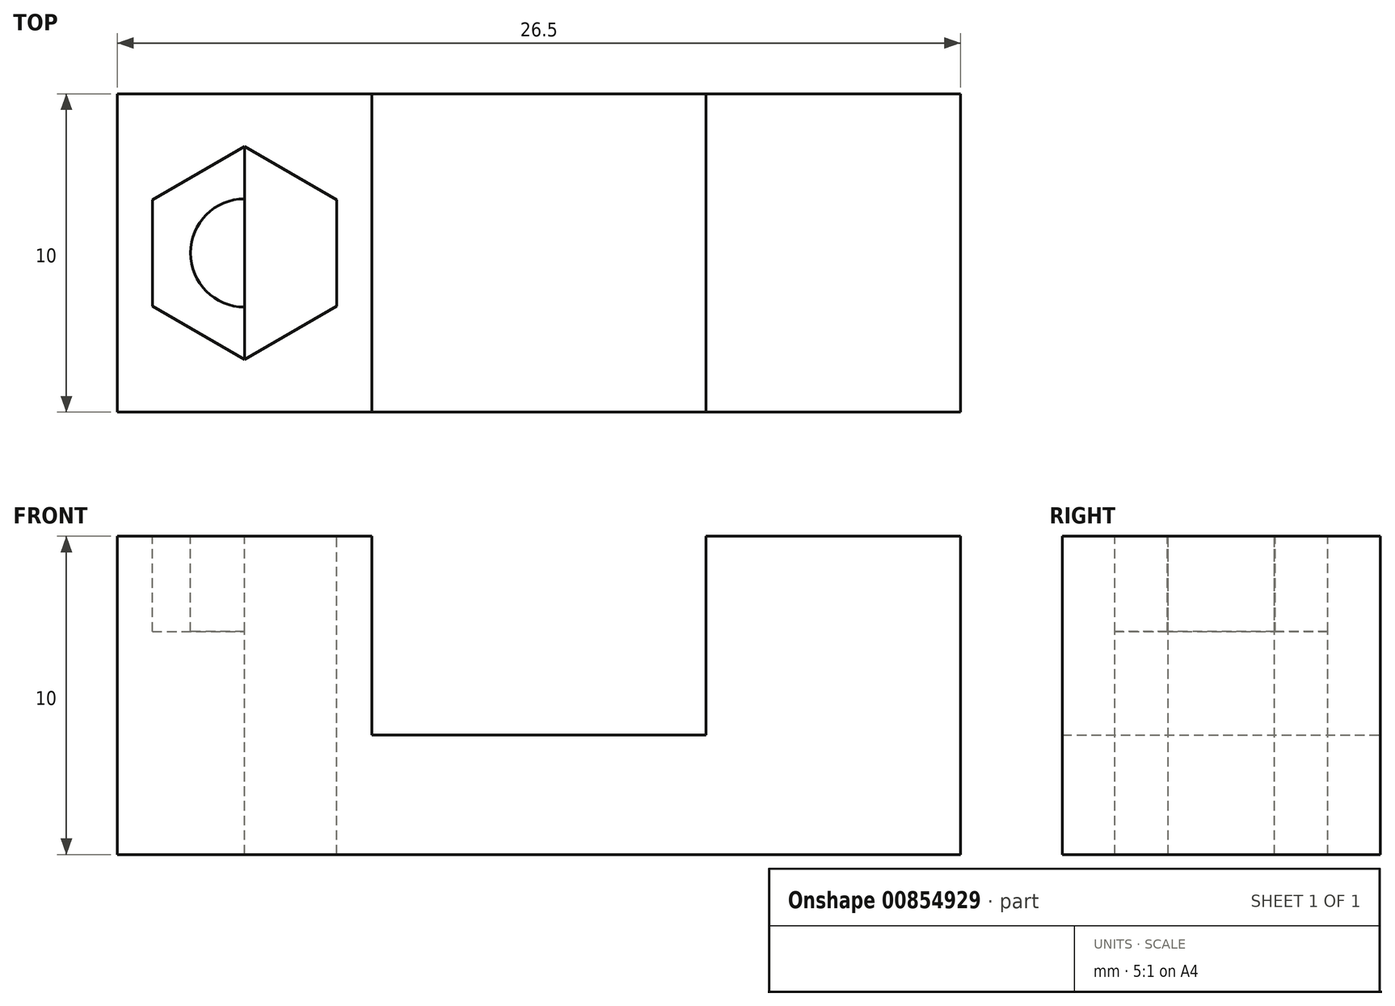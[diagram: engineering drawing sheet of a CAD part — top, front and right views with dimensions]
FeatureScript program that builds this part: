
annotation { "Feature Type Name" : "Feature", "Feature Type Description" : "" }
export const myFeature = defineFeature(function(context is Context, id is Id, definition is map)
    precondition{}
    {
        {
            var Q0;
            Q0=qCreatedBy(makeId("Front.planeOp"),FACE);
            var sketch = newSketch(context, id + "F0", { "sketchPlane" : qUnion([Q0])});
            skLineSegment(sketch, "E0", {"start": v(0, -6.25) * mm, "end": v(-5.25, -6.25) * mm});
            skLineSegment(sketch, "E1", {"start": v(-5.25, -6.25) * mm, "end": v(-5.25, 0) * mm});
            skLineSegment(sketch, "E2", {"start": v(-5.25, 0) * mm, "end": v(-13.25, 0) * mm});
            skLineSegment(sketch, "E3", {"start": v(-13.25, 0) * mm, "end": v(-13.25, -10) * mm});
            skLineSegment(sketch, "E4", {"start": v(-13.25, -10) * mm, "end": v(0, -10) * mm});
            skLineSegment(sketch, "E5", {"start": v(0, -6.25) * mm, "end": v(0, -10) * mm});
            skLineSegment(sketch, "E6.MirrorCS", {"start": v(0, -6.25) * mm, "end": v(5.25, -6.25) * mm});
            skLineSegment(sketch, "E7.MirrorCS", {"start": v(5.25, -6.25) * mm, "end": v(5.25, 0) * mm});
            skLineSegment(sketch, "E8.MirrorCS", {"start": v(5.25, 0) * mm, "end": v(13.25, 0) * mm});
            skLineSegment(sketch, "E9.MirrorCS", {"start": v(13.25, 0) * mm, "end": v(13.25, -10) * mm});
            skLineSegment(sketch, "E10.MirrorCS", {"start": v(13.25, -10) * mm, "end": v(0, -10) * mm});
            skSolve(sketch);
        }
        {
            var Q0;
            Q0 = qSketchRegion(id + "F0", true);
            extrude(context, id + "F1", {"entities" : qUnion([Q0]), "depth" : 10 * mm, "offsetDistance" : 25 * mm});
        }
        {
            var Q0;
            Q0=makeQuery(id+"F1.opExtrude","SWEPT_FACE",FACE,{"disambiguationData":[OSD([sQuery(id+"F0.wireOp",EDGE,"E2")])]});
            var sketch = newSketch(context, id + "F2", { "sketchPlane" : qUnion([Q0])});
            skLineSegment(sketch, "E11", {"start": v(-15.32, -5) * mm, "end": v(-4.16, -5) * mm});
            skPoint(sketch, "E11.startSnap0", {"position": v(-13.25, -5) * mm});
            skLineSegment(sketch, "E12", {"start": v(-9.25, -11.56) * mm, "end": v(-9.25, 1.56) * mm});
            skPoint(sketch, "E12.startSnap0", {"position": v(-9.25, -10) * mm});
            skCircle(sketch, "E13", {"center": v(-9.25, -5) * mm, "radius": 1.7 * mm});
            skCircle(sketch, "E14.cCircle", {"center": v(-9.25, -5) * mm, "radius": 2.9 * mm, "construction": true});
            skLineSegment(sketch, "E14.0", {"start": v(-6.35, -3.33) * mm, "end": v(-6.35, -6.67) * mm});
            skLineSegment(sketch, "E14.1", {"start": v(-6.35, -6.67) * mm, "end": v(-9.25, -8.35) * mm});
            skLineSegment(sketch, "E14.2", {"start": v(-9.25, -8.35) * mm, "end": v(-12.15, -6.67) * mm});
            skLineSegment(sketch, "E14.3", {"start": v(-12.15, -6.67) * mm, "end": v(-12.15, -3.33) * mm});
            skLineSegment(sketch, "E14.4", {"start": v(-12.15, -3.33) * mm, "end": v(-9.25, -1.65) * mm});
            skLineSegment(sketch, "E14.5", {"start": v(-9.25, -1.65) * mm, "end": v(-6.35, -3.33) * mm});
            skPoint(sketch, "E14.0.midPoint", {"position": v(-6.35, -5) * mm});
            skSolve(sketch);
        }
        {
            var Q0;
            {var subQ0=sQuery(id+"F2.wireOp",EDGE,"E13");var subQ1=sQuery(id+"F2.wireOp",EDGE,"E11");var subQ2=makeQuery(id+"F2.imprint","INTERSECT",VERTEX,{"disambiguationData":[OD(0.0)],"derivedFrom":[subQ1,subQ0]});Q0=makeQuery(id+"F2.imprint","IMPRINT",FACE,{"disambiguationData":[TD([[makeQuery(id+"F2.imprint","IMPRINT",EDGE,{"disambiguationData":[TD([[subQ2,-1.0]])],"derivedFrom":subQ1}),1.0]])]});}
            var Q1;
            {var subQ0=sQuery(id+"F2.wireOp",EDGE,"E12");var subQ1=sQuery(id+"F2.wireOp",EDGE,"E11");var subQ2=makeQuery(id+"F2.imprint","INTERSECT",VERTEX,{"derivedFrom":[subQ1,subQ0]});Q1=makeQuery(id+"F2.imprint","IMPRINT",FACE,{"disambiguationData":[TD([[makeQuery(id+"F2.imprint","IMPRINT",EDGE,{"disambiguationData":[TD([[subQ2,-1.0]])],"derivedFrom":subQ1}),1.0]])]});}
            var Q2;
            {var subQ0=sQuery(id+"F2.wireOp",EDGE,"E12");var subQ1=sQuery(id+"F2.wireOp",EDGE,"E11");var subQ2=makeQuery(id+"F2.imprint","INTERSECT",VERTEX,{"derivedFrom":[subQ1,subQ0]});Q2=makeQuery(id+"F2.imprint","IMPRINT",FACE,{"disambiguationData":[TD([[makeQuery(id+"F2.imprint","IMPRINT",EDGE,{"disambiguationData":[TD([[subQ2,-1.0]])],"derivedFrom":subQ1}),-1.0]])]});}
            var Q3;
            {var subQ0=sQuery(id+"F2.wireOp",EDGE,"E13");var subQ1=sQuery(id+"F2.wireOp",EDGE,"E11");var subQ2=makeQuery(id+"F2.imprint","INTERSECT",VERTEX,{"disambiguationData":[OD(0.0)],"derivedFrom":[subQ1,subQ0]});Q3=makeQuery(id+"F2.imprint","IMPRINT",FACE,{"disambiguationData":[TD([[makeQuery(id+"F2.imprint","IMPRINT",EDGE,{"disambiguationData":[TD([[subQ2,-1.0]])],"derivedFrom":subQ1}),-1.0]])]});}
            extrude(context, id + "F3", {"entities" : qUnion([Q0, Q1, Q2, Q3]), "operationType" : NewBodyOperationType.REMOVE, "endBound" : BoundingType.THROUGH_ALL, "oppositeDirection" : true, "depth" : 25 * mm, "offsetDistance" : 25 * mm});
        }
        {
            var Q0;
            Q0 = qSketchRegion(id + "F2", true);
            extrude(context, id + "F4", {"entities" : qUnion([Q0]), "operationType" : NewBodyOperationType.REMOVE, "oppositeDirection" : true, "depth" : 3 * mm, "offsetDistance" : 25 * mm});
        }
    });
